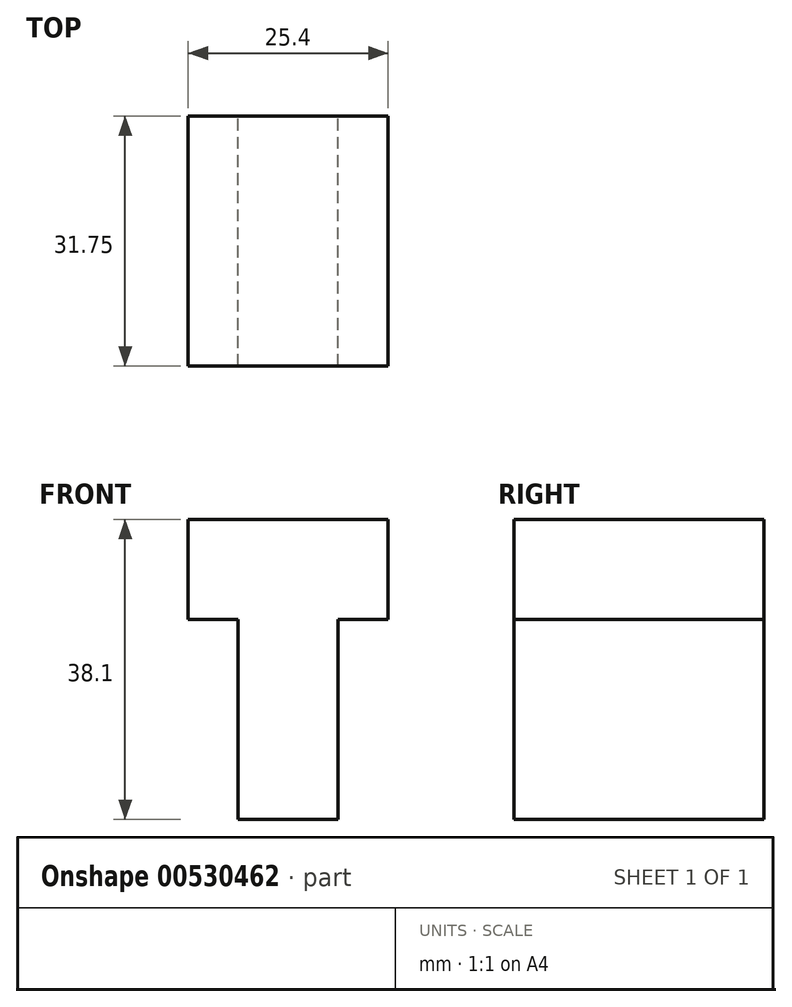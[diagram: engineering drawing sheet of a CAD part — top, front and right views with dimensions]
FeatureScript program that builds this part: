
annotation { "Feature Type Name" : "Feature", "Feature Type Description" : "" }
export const myFeature = defineFeature(function(context is Context, id is Id, definition is map)
    precondition{}
    {
        {
            var Q0;
            Q0=qCreatedBy(makeId("Front.planeOp"),FACE);
            var sketch = newSketch(context, id + "F0", { "sketchPlane" : qUnion([Q0])});
            skLineSegment(sketch, "E0", {"start": v(-25.3, 0) * mm, "end": v(-25.3, 25.4) * mm});
            skLineSegment(sketch, "E1", {"start": v(-25.3, 25.4) * mm, "end": v(-31.65, 25.4) * mm});
            skLineSegment(sketch, "E2", {"start": v(-31.65, 25.4) * mm, "end": v(-31.65, 38.1) * mm});
            skLineSegment(sketch, "E3", {"start": v(-12.6, 25.4) * mm, "end": v(-12.6, 0) * mm});
            skLineSegment(sketch, "E4", {"start": v(-12.6, 25.4) * mm, "end": v(-6.25, 25.4) * mm});
            skLineSegment(sketch, "E5", {"start": v(-6.25, 25.4) * mm, "end": v(-6.25, 38.1) * mm});
            skLineSegment(sketch, "E6", {"start": v(-25.3, 0) * mm, "end": v(-12.6, 0) * mm});
            skLineSegment(sketch, "E7", {"start": v(-31.65, 38.1) * mm, "end": v(-6.25, 38.1) * mm});
            skSolve(sketch);
        }
        {
            var Q0;
            Q0 = qSketchRegion(id + "F0", true);
            extrude(context, id + "F1", {"entities" : qUnion([Q0]), "depth" : 31.75 * mm, "offsetDistance" : 25.4 * mm});
        }
    });
